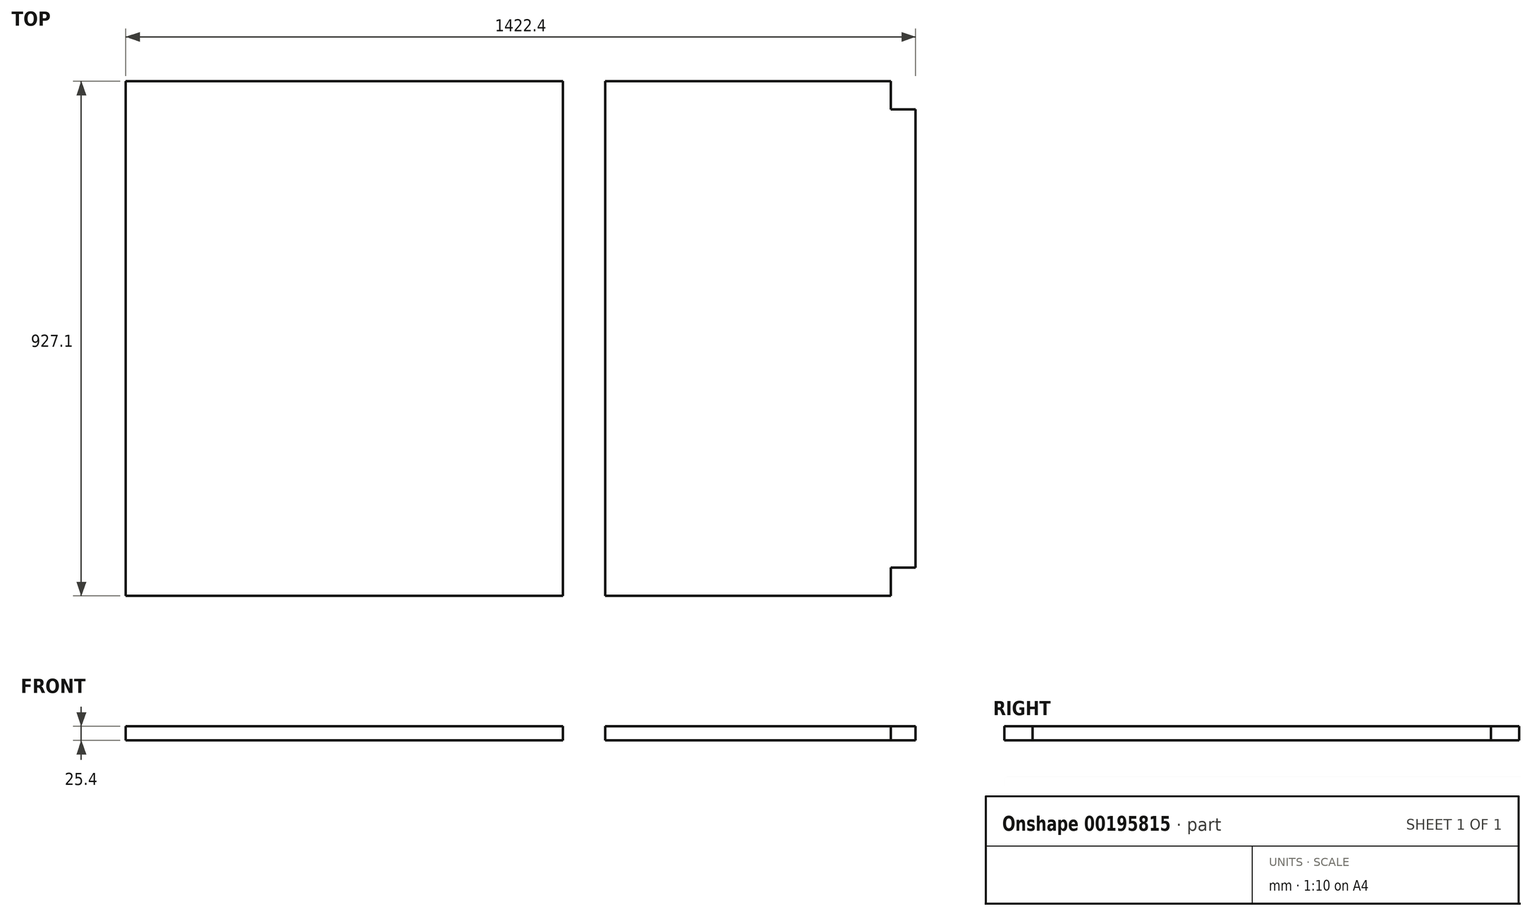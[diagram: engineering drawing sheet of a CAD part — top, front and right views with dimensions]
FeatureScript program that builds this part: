
annotation { "Feature Type Name" : "Feature", "Feature Type Description" : "" }
export const myFeature = defineFeature(function(context is Context, id is Id, definition is map)
    precondition{}
    {
        {
            var Q0;
            Q0=qCreatedBy(makeId("Top.planeOp"),FACE);
            var sketch = newSketch(context, id + "F0", { "sketchPlane" : qUnion([Q0])});
            skLineSegment(sketch, "E0.bottom", {"start": v(0, 0) * mm, "end": v(787.4, 0) * mm});
            skLineSegment(sketch, "E0.top", {"start": v(0, 927.1) * mm, "end": v(787.4, 927.1) * mm});
            skLineSegment(sketch, "E0.left", {"start": v(0, 0) * mm, "end": v(0, 927.1) * mm});
            skLineSegment(sketch, "E0.right", {"start": v(787.4, 0) * mm, "end": v(787.4, 927.1) * mm});
            skLineSegment(sketch, "E1.bottom", {"start": v(863.6, 0) * mm, "end": v(1377.95, 0) * mm});
            skLineSegment(sketch, "E1.top", {"start": v(863.6, 927.1) * mm, "end": v(1377.95, 927.1) * mm});
            skLineSegment(sketch, "E1.left", {"start": v(863.6, 0) * mm, "end": v(863.6, 927.1) * mm});
            skLineSegment(sketch, "E1.right", {"start": v(1422.4, 50.8) * mm, "end": v(1422.4, 876.3) * mm});
            skLineSegment(sketch, "E2", {"start": v(1377.95, 927.1) * mm, "end": v(1377.95, 876.3) * mm});
            skLineSegment(sketch, "E3", {"start": v(1377.95, 876.3) * mm, "end": v(1422.4, 876.3) * mm});
            skLineSegment(sketch, "E4", {"start": v(1422.4, 50.8) * mm, "end": v(1377.95, 50.8) * mm});
            skLineSegment(sketch, "E5", {"start": v(1377.95, 50.8) * mm, "end": v(1377.95, 0) * mm});
            skSolve(sketch);
        }
        {
            var Q0;
            Q0 = qSketchRegion(id + "F0", true);
            extrude(context, id + "F1", {"entities" : qUnion([Q0]), "depth" : 25.4 * mm});
        }
    });
